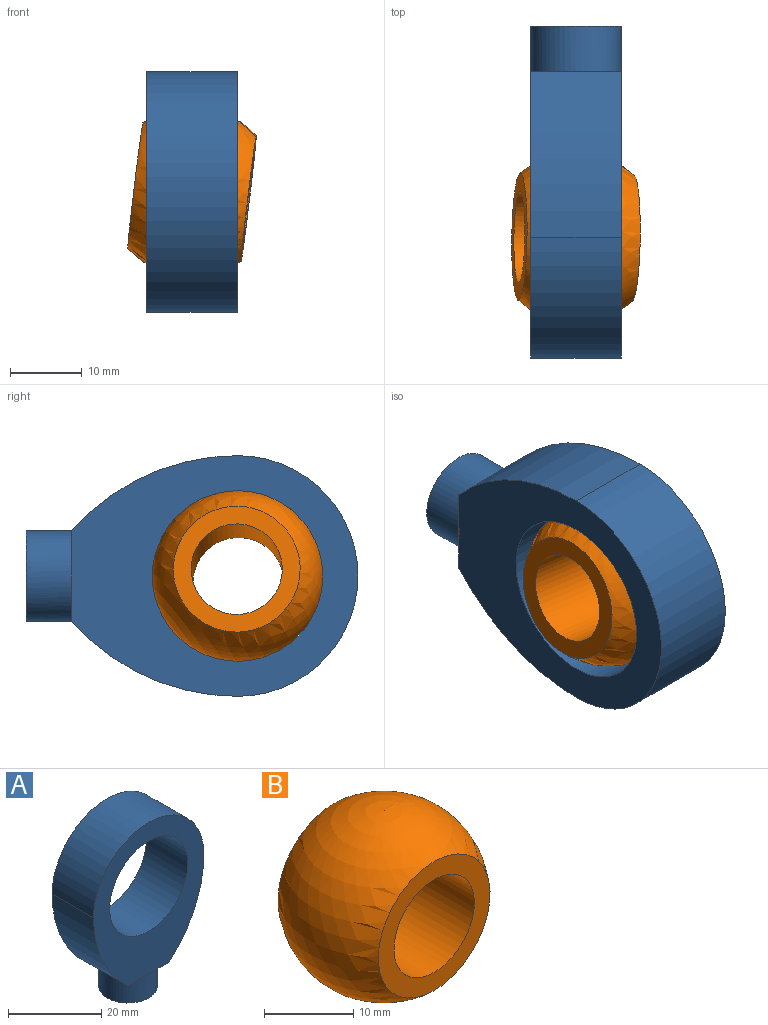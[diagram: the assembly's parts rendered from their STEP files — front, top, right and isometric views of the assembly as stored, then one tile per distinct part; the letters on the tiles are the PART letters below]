
ASSEMBLY  parts=2 mates=1
PART A: 12 faces, bbox 33.5x12.6x46.2 mm
  f0: plane 6.29x6.29mm, normal (0,0,-1), area 8.5mm2, adj f7,f9,f10
  f1: plane 6.29x6.29mm, normal (0,0,-1), area 8.5mm2, adj f4,f9,f10
  f2: plane 6.29x6.29mm, normal (0,0,-1), area 8.5mm2, adj f4,f8,f10
  f3: plane 6.29x6.29mm, normal (0,0,-1), area 8.5mm2, adj f7,f8,f10
  f4: cylinder r=30.73mm len=23.11mm, axis (0,1,0), area 328.9mm2, adj f1,f2,f5,f8,f9
  f5: cylinder r=16.76mm len=33.53mm, axis (0,1,0), area 662.2mm2, adj f4,f7,f8,f9
  f6: cylinder r=11.87mm len=23.75mm, axis (0,1,0), area 938.1mm2, adj f8,f9
  f7: cylinder r=30.73mm len=23.11mm, axis (0,1,0), area 328.9mm2, adj f0,f3,f5,f8,f9
  f8: plane 39.88x33.53mm, normal (0,-1,0), area 624.9mm2, adj f2,f3,f4,f5,f6,f7
  f9: plane 39.88x33.53mm, normal (0,1,0), area 624.9mm2, adj f0,f1,f4,f5,f6,f7
  f10: cylinder r=6.29mm len=12.57mm, axis (0,0,1), area 250.8mm2, adj f0,f1,f2,f3,f11
  f11: plane 12.57x12.57mm, normal (0,0,-1), area 124.2mm2, adj f10
PART B: 4 faces, bbox 23.7x23.7x23.7 mm
  f0: sphere r=11.87mm, area 1185mm2, adj f1,f2
  f1: plane 17.66x17.66mm, normal (0,-1,0), area 118.4mm2, adj f0,f3
  f2: plane 17.65x17.65mm, normal (0,1,0), area 118mm2, adj f0,f3
  f3: cylinder r=6.35mm len=15.88mm, axis (0,1,0), area 633.7mm2, adj f1,f2
PLACE A rot(axis=(0.58,0.58,-0.58),120deg) t=(3.06,-7.98,-5.95)mm fixed
PLACE B rot(axis=(-0.7,-0.65,-0.29),140deg) t=(3.06,-7.98,-5.95)mm
MATE ball B.f3 <-> A.f6  axis (0.99,-0.02,-0.12) through (3.06,-7.98,-5.95)mm
